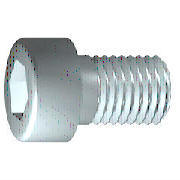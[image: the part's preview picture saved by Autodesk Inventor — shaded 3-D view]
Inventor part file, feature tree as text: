
AUTODESK INVENTOR PART (.ipt)
format: ipt  version: 2018 (Build 220112000, 112)  size: 189,440 bytes
history: native  units: mm (DEFAULTED — no unit token found)
features: sketch x2, extrude x1, plane x1, fillet x1
ambient origin geometry x7: Origin, YZ Plane, XY Plane, X Axis, Y Axis, Z Axis, Center Point
bodies: Solid1 (feature_tree), Body (feature_tree)
feature tree (5):
  extrude  "Slot"  Depth=3.0mm
  plane  "Work Plane1"
  fillet  "Fillet2"  Radius=3.0mm
  sketch  "Sketch1"  dims[d1=10.693275mm d2=0.306825mm d3=3.0mm]
  sketch  "Sketch2"  dims[d4=1.5mm d5=60.0deg d6=3.0mm d7=3.0mm d8=2.886751mm d9=5.5mm d10=90.0deg d11=10.0mm d12=0.0mm d13=10.693275mm d14=0.0mm d15=0.306725mm d16=0.306725mm d17=0.3mm d19=0.0mm d26=12.0mm d27=45.0deg d28=0.0mm d29=0.0mm d30=0.1mm]
